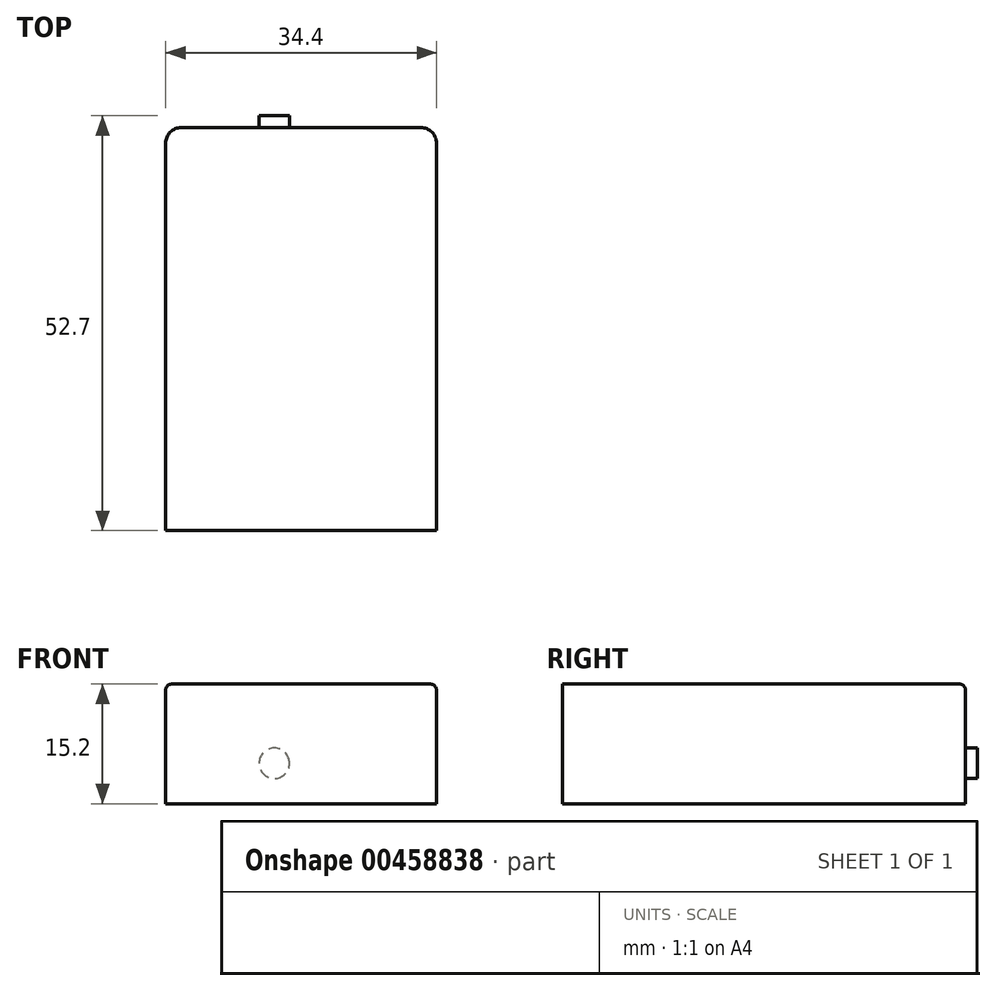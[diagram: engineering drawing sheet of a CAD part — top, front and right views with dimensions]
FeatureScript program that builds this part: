
annotation { "Feature Type Name" : "Feature", "Feature Type Description" : "" }
export const myFeature = defineFeature(function(context is Context, id is Id, definition is map)
    precondition{}
    {
        {
            var Q0;
            Q0=qCreatedBy(makeId("Front.planeOp"),FACE);
            var sketch = newSketch(context, id + "F0", { "sketchPlane" : qUnion([Q0])});
            skLineSegment(sketch, "E0.bottom", {"start": v(0, 0) * mm, "end": v(34.4, 0) * mm});
            skLineSegment(sketch, "E0.top", {"start": v(0, 15.2) * mm, "end": v(34.4, 15.2) * mm});
            skLineSegment(sketch, "E0.left", {"start": v(0, 0) * mm, "end": v(0, 15.2) * mm});
            skLineSegment(sketch, "E0.right", {"start": v(34.4, 0) * mm, "end": v(34.4, 15.2) * mm});
            skPoint(sketch, "E1.centerSnap0", {"position": v(17.2, 15.2) * mm});
            skPoint(sketch, "E1.centerSnap1", {"position": v(34.4, 7.6) * mm});
            skPoint(sketch, "E2.centerSnap0", {"position": v(17.2, 0) * mm});
            skCircle(sketch, "E3", {"center": v(13.8, 5.15) * mm, "radius": 1.94 * mm});
            skSolve(sketch);
        }
        {
            var Q0;
            Q0=makeQuery(id+"F0.imprint","IMPRINT",FACE,{"disambiguationData":[TD([[makeQuery(id+"F0.imprint","IMPRINT",EDGE,{"derivedFrom":sQuery(id+"F0.wireOp",EDGE,"E3")}),1.0]])]});
            var Q1;
            Q1=makeQuery(id+"F0.imprint","IMPRINT",FACE,{"disambiguationData":[TD([[makeQuery(id+"F0.imprint","IMPRINT",EDGE,{"derivedFrom":sQuery(id+"F0.wireOp",EDGE,"E0.bottom")}),1.0]])]});
            extrude(context, id + "F1", {"entities" : qUnion([Q0, Q1]), "depth" : 51.2 * mm, "offsetDistance" : 25 * mm});
        }
        {
            var Q0;
            Q0=makeQuery(id+"F0.imprint","IMPRINT",FACE,{"disambiguationData":[TD([[makeQuery(id+"F0.imprint","IMPRINT",EDGE,{"derivedFrom":sQuery(id+"F0.wireOp",EDGE,"E3")}),1.0]])]});
            extrude(context, id + "F2", {"entities" : qUnion([Q0]), "operationType" : NewBodyOperationType.ADD, "oppositeDirection" : true, "depth" : 1.5 * mm, "offsetDistance" : 25 * mm});
        }
        {
            var Q0;
            Q0=makeQuery(id+"F1.opExtrude","CAP_EDGE",EDGE,{"disambiguationData":[OSD([sQuery(id+"F0.wireOp",EDGE,"E0.right")])],"isStart":true});
            var Q1;
            Q1=makeQuery(id+"F1.opExtrude","CAP_EDGE",EDGE,{"disambiguationData":[OSD([sQuery(id+"F0.wireOp",EDGE,"E0.left")])],"isStart":true});
            fillet(context, id + "F3", {"entities" : qUnion([Q0, Q1]), "radius" : 2 * mm, "tangentPropagation" : true, "allowEdgeOverflow" : false});
        }
        {
            var Q0;
            Q0=makeQuery(id+"F1.opExtrude","SWEPT_EDGE",EDGE,{"disambiguationData":[OSD([sQuery(id+"F0.wireOp",EDGE,"E0.top"),sQuery(id+"F0.wireOp",EDGE,"E0.right")])]});
            fillet(context, id + "F4", {"entities" : qUnion([Q0]), "radius" : 0.75 * mm, "tangentPropagation" : true, "allowEdgeOverflow" : false});
        }
    });
